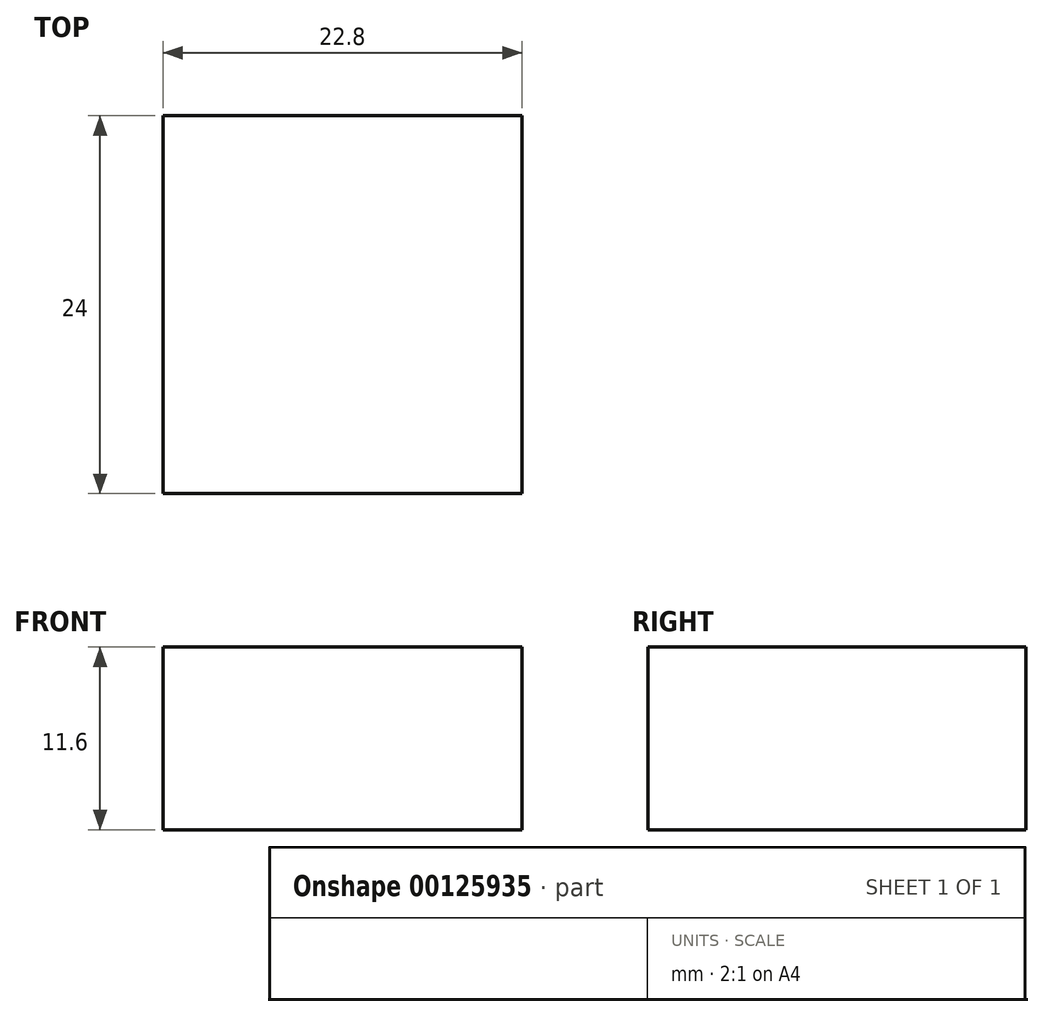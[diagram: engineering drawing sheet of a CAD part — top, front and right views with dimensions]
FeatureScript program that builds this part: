
annotation { "Feature Type Name" : "Feature", "Feature Type Description" : "" }
export const myFeature = defineFeature(function(context is Context, id is Id, definition is map)
    precondition{}
    {
        {
            var Q0;
            Q0=qCreatedBy(makeId("Front.planeOp"),FACE);
            var sketch = newSketch(context, id + "F0", { "sketchPlane" : qUnion([Q0])});
            skLineSegment(sketch, "E0.bottom", {"start": v(-63.05, 34.91) * mm, "end": v(-40.25, 34.91) * mm});
            skLineSegment(sketch, "E0.top", {"start": v(-63.05, 23.31) * mm, "end": v(-40.25, 23.31) * mm});
            skLineSegment(sketch, "E0.left", {"start": v(-63.05, 34.91) * mm, "end": v(-63.05, 23.31) * mm});
            skLineSegment(sketch, "E0.right", {"start": v(-40.25, 34.91) * mm, "end": v(-40.25, 23.31) * mm});
            skSolve(sketch);
        }
        {
            var Q0;
            Q0=qSketchRegion(id+"F0",true);
            extrude(context, id + "F1", {"entities" : qUnion([Q0]), "depth" : 24 * mm});
        }
    });
